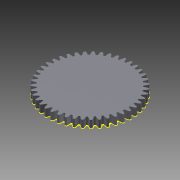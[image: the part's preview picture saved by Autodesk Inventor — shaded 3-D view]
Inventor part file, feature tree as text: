
AUTODESK INVENTOR PART (.ipt)
format: ipt  version: 2014 (Build 180170000, 170)  size: 371,200 bytes
history: native  units: mm (DEFAULTED — no unit token found)
features: plane x4, sketch x4, extrude x3, other x3, mirror x1
ambient origin geometry x8: Origin, YZ Plane, XZ Plane, XY Plane, X Axis, Y Axis, Z Axis, Center Point
bodies: Solid1 (feature_tree)
feature tree (15):
  extrude  "Extrusion1"  Depth=8.0mm TaperAngle=0.0deg
  plane  "Work Plane2"
  plane  "Work Plane8"
  plane  "Work Plane9"
  other  "Spur Gear"
  extrude  "Extrusion2"  Depth=10.0mm TaperAngle=0.0deg
  plane  "Work Plane11"
  mirror  "Mirror1"
  extrude  "Extrusion3"  Depth=0.730603mm TaperAngle=0.0deg
  sketch  "Sketch1"  dims[d0=90.0mm d1=8.0mm d2=0.0mm]
  sketch  "Sketch2"  dims[d3=86.0mm d4=10.0mm d5=0.0mm]
  other  "Srf1"
  sketch  "Sketch3"  dims[d16=66.0mm d17=0.0mm d34=0.730603mm]
  sketch  "Sketch4"  dims[d39=0.0mm d41=0.0mm d43=66.0mm d46=66.0mm d47=0.0mm d48=0.0mm d49=5.0mm d50=7.0mm d51=3.0mm d52=2.5mm d53=0.0mm d54=5.0mm d55=0.0mm]
  other  "Pitch Diameter"
